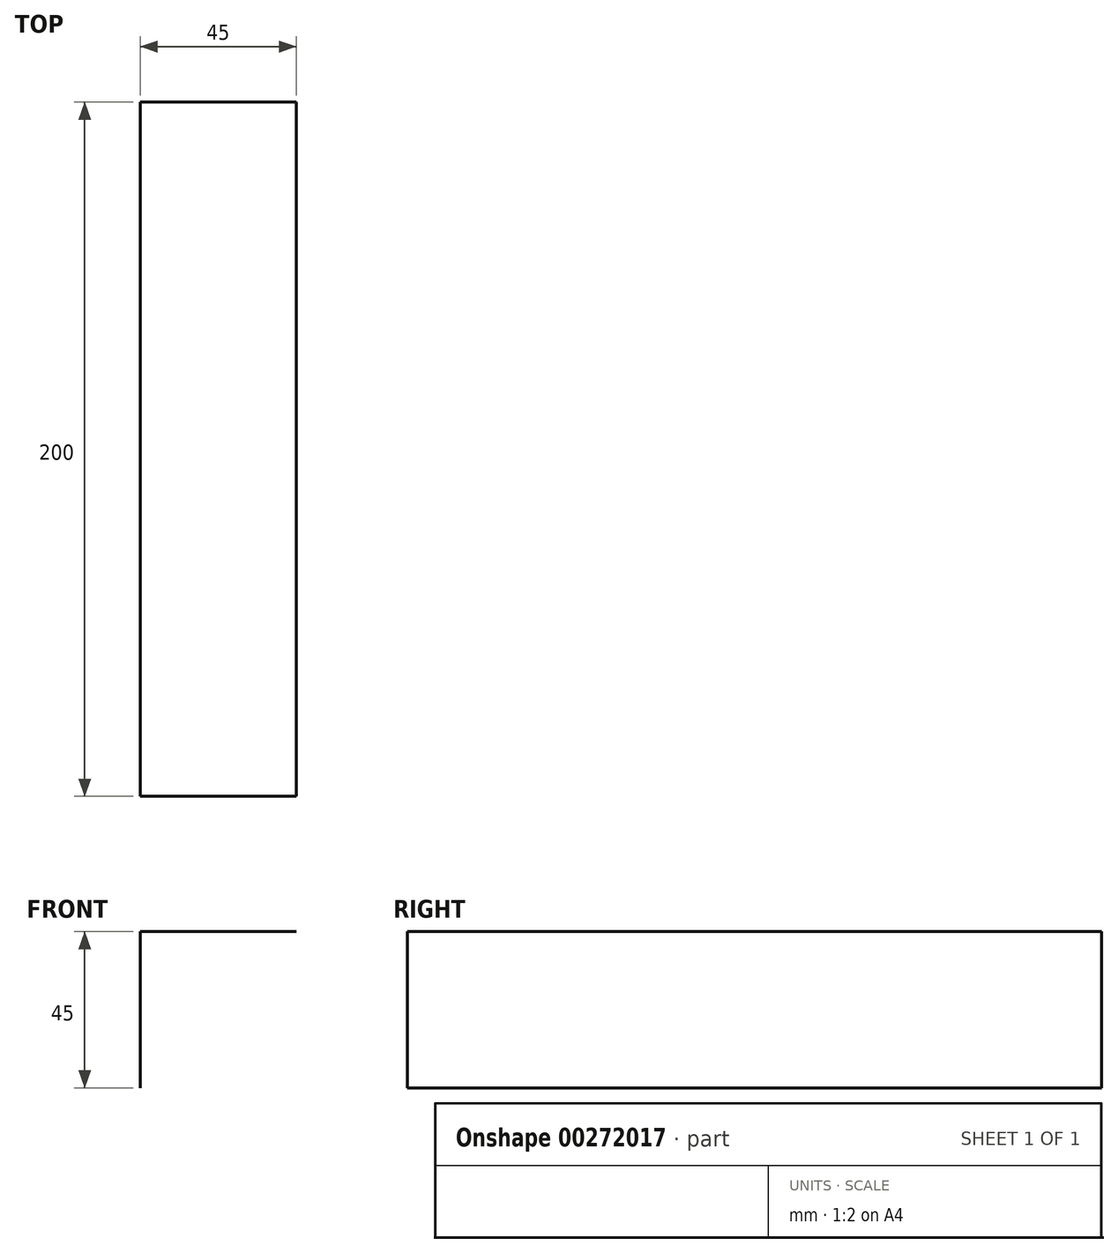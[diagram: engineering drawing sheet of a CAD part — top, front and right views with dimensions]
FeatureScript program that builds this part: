
annotation { "Feature Type Name" : "Feature", "Feature Type Description" : "" }
export const myFeature = defineFeature(function(context is Context, id is Id, definition is map)
    precondition{}
    {
        {
            var Q0;
            Q0=qCreatedBy(makeId("Front.planeOp"),FACE);
            var sketch = newSketch(context, id + "F0", { "sketchPlane" : qUnion([Q0])});
            skLineSegment(sketch, "E0", {"start": v(0, 0) * mm, "end": v(0, -45) * mm});
            skLineSegment(sketch, "E1", {"start": v(0, 0) * mm, "end": v(45, 0) * mm});
            skSolve(sketch);
        }
        {
            var Q0;
            Q0=sQuery(id+"F0.wireOp",EDGE,"E0");
            var Q1;
            Q1=sQuery(id+"F0.wireOp",EDGE,"E1");
            extrude(context, id + "F1", {"bodyType" : ToolBodyType.SURFACE, "surfaceEntities" : qUnion([Q0, Q1]), "oppositeDirection" : true, "depth" : 200 * mm});
        }
    });
